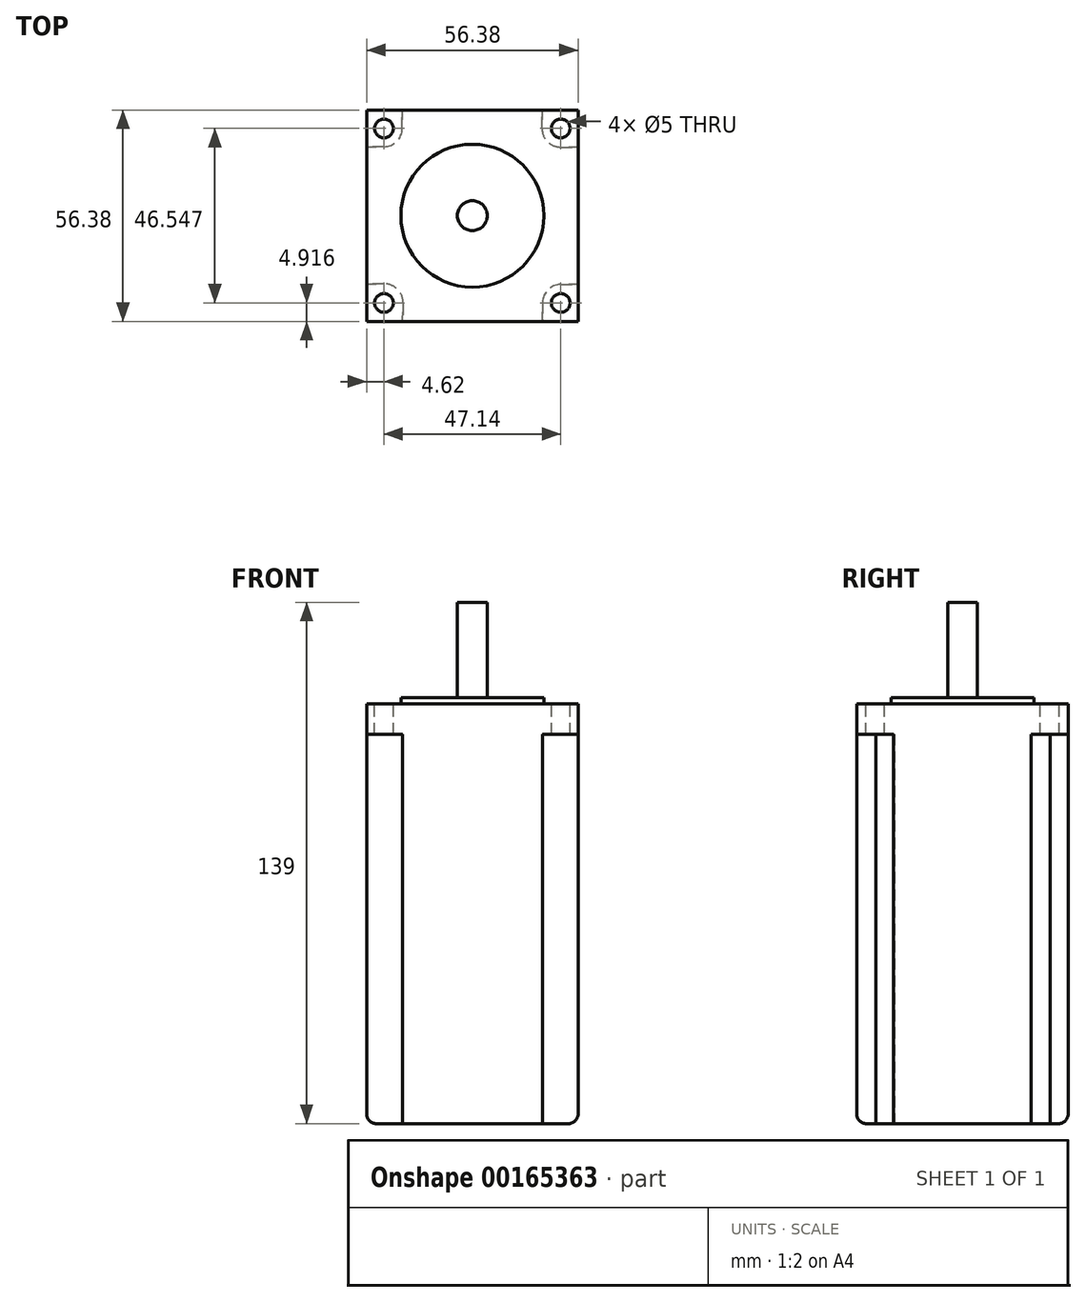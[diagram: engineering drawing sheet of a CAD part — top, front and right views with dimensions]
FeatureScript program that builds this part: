
annotation { "Feature Type Name" : "Feature", "Feature Type Description" : "" }
export const myFeature = defineFeature(function(context is Context, id is Id, definition is map)
    precondition{}
    {
        {
            var Q0;
            Q0=qCreatedBy(makeId("Top.planeOp"),FACE);
            var sketch = newSketch(context, id + "F0", { "sketchPlane" : qUnion([Q0])});
            skLineSegment(sketch, "E0.rect.bottom", {"start": v(28.2, -28.2) * mm, "end": v(-28.2, -28.2) * mm});
            skLineSegment(sketch, "E0.rect.top", {"start": v(28.2, 28.2) * mm, "end": v(-28.2, 28.2) * mm});
            skLineSegment(sketch, "E0.rect.left", {"start": v(28.2, -28.2) * mm, "end": v(28.2, 28.2) * mm});
            skLineSegment(sketch, "E0.rect.right", {"start": v(-28.2, -28.2) * mm, "end": v(-28.2, 28.2) * mm});
            skPoint(sketch, "E0.rect.middle", {"position": v(0, 0) * mm});
            skSolve(sketch);
        }
        {
            var Q0;
            Q0=qSketchRegion(id+"F0",true);
            extrude(context, id + "F1", {"entities" : qUnion([Q0]), "depth" : 112 * mm});
        }
        {
            var Q0;
            Q0=makeQuery(id+"F1.opExtrude","CAP_FACE",FACE,{"disambiguationData":[OSD([sQuery(id+"F0.wireOp",EDGE,"E0.rect.bottom"),sQuery(id+"F0.wireOp",EDGE,"E0.rect.top"),sQuery(id+"F0.wireOp",EDGE,"E0.rect.left"),sQuery(id+"F0.wireOp",EDGE,"E0.rect.right")])],"isStart":false});
            var sketch = newSketch(context, id + "F2", { "sketchPlane" : qUnion([Q0])});
            skLineSegment(sketch, "E1.rect.bottom", {"start": v(23.57, 23.27) * mm, "end": v(-23.57, 23.27) * mm, "construction": true});
            skLineSegment(sketch, "E1.rect.top", {"start": v(23.57, -23.27) * mm, "end": v(-23.57, -23.27) * mm, "construction": true});
            skLineSegment(sketch, "E1.rect.left", {"start": v(23.57, 23.27) * mm, "end": v(23.57, -23.27) * mm, "construction": true});
            skLineSegment(sketch, "E1.rect.right", {"start": v(-23.57, 23.27) * mm, "end": v(-23.57, -23.27) * mm, "construction": true});
            skPoint(sketch, "E1.rect.middle", {"position": v(0, 0) * mm});
            skCircle(sketch, "E2", {"center": v(-23.57, 23.27) * mm, "radius": 2.5 * mm});
            skCircle(sketch, "E3", {"center": v(23.57, 23.27) * mm, "radius": 2.5 * mm});
            skCircle(sketch, "E4", {"center": v(23.57, -23.27) * mm, "radius": 2.5 * mm});
            skCircle(sketch, "E5", {"center": v(-23.57, -23.27) * mm, "radius": 2.5 * mm});
            skSolve(sketch);
        }
        {
            var Q0;
            Q0=qSketchRegion(id+"F2",true);
            extrude(context, id + "F3", {"entities" : qUnion([Q0]), "operationType" : NewBodyOperationType.REMOVE, "endBound" : BoundingType.THROUGH_ALL, "oppositeDirection" : true, "depth" : 25.4 * mm});
        }
        {
            var Q0;
            Q0=makeQuery(id+"F1.opExtrude","CAP_FACE",FACE,{"disambiguationData":[OSD([sQuery(id+"F0.wireOp",EDGE,"E0.rect.bottom"),sQuery(id+"F0.wireOp",EDGE,"E0.rect.top"),sQuery(id+"F0.wireOp",EDGE,"E0.rect.left"),sQuery(id+"F0.wireOp",EDGE,"E0.rect.right")])],"isStart":false});
            var sketch = newSketch(context, id + "F4", { "sketchPlane" : qUnion([Q0])});
            skCircle(sketch, "E6", {"center": v(0, 0) * mm, "radius": 19.05 * mm});
            skSolve(sketch);
        }
        {
            var Q0;
            Q0=qSketchRegion(id+"F4",true);
            extrude(context, id + "F5", {"entities" : qUnion([Q0]), "operationType" : NewBodyOperationType.ADD, "depth" : 1.6 * mm});
        }
        {
            var Q0;
            Q0=makeQuery(id+"F5.opExtrude","CAP_FACE",FACE,{"disambiguationData":[OSD([sQuery(id+"F4.wireOp",EDGE,"E6")])],"isStart":false});
            var sketch = newSketch(context, id + "F6", { "sketchPlane" : qUnion([Q0])});
            skCircle(sketch, "E7", {"center": v(0, 0) * mm, "radius": 3.97 * mm});
            skSolve(sketch);
        }
        {
            var Q0;
            Q0=qSketchRegion(id+"F6",true);
            extrude(context, id + "F7", {"entities" : qUnion([Q0]), "operationType" : NewBodyOperationType.ADD, "depth" : 25.4 * mm});
        }
        {
            var Q0;
            Q0=makeQuery(id+"F1.opExtrude","CAP_FACE",FACE,{"disambiguationData":[OSD([sQuery(id+"F0.wireOp",EDGE,"E0.rect.bottom"),sQuery(id+"F0.wireOp",EDGE,"E0.rect.top"),sQuery(id+"F0.wireOp",EDGE,"E0.rect.left"),sQuery(id+"F0.wireOp",EDGE,"E0.rect.right")])],"isStart":true});
            var sketch = newSketch(context, id + "F8", { "sketchPlane" : qUnion([Q0])});
            skCircle(sketch, "E8", {"center": v(-23.57, 23.27) * mm, "radius": 5.12 * mm, "construction": true});
            skCircle(sketch, "E9", {"center": v(23.57, 23.27) * mm, "radius": 4.9 * mm, "construction": true});
            skCircle(sketch, "E10", {"center": v(23.57, -23.27) * mm, "radius": 5 * mm, "construction": true});
            skCircle(sketch, "E11", {"center": v(-23.57, -23.27) * mm, "radius": 4.87 * mm, "construction": true});
            skLineSegment(sketch, "E12", {"start": v(-18.46, 23.44) * mm, "end": v(-18.61, 28.2) * mm});
            skLineSegment(sketch, "E13", {"start": v(-23.6, 18.16) * mm, "end": v(-28.2, 18.16) * mm});
            skArc(sketch, "E14", {"start": v(-23.6, 18.16) * mm, "mid": v(-19.91, 19.71) * mm, "end": v(-18.46, 23.44) * mm});
            skLineSegment(sketch, "E15", {"start": v(-28.2, 18.16) * mm, "end": v(-28.2, 28.2) * mm});
            skLineSegment(sketch, "E16", {"start": v(-28.2, 28.2) * mm, "end": v(-18.61, 28.2) * mm});
            skLineSegment(sketch, "E17", {"start": v(-18.7, -23.27) * mm, "end": v(-18.7, -28.2) * mm});
            skLineSegment(sketch, "E18", {"start": v(-18.7, -28.2) * mm, "end": v(-19.13, -28.28) * mm});
            skLineSegment(sketch, "E19", {"start": v(-23.57, -18.4) * mm, "end": v(-28.2, -18.4) * mm});
            skLineSegment(sketch, "E20", {"start": v(18.58, -23.35) * mm, "end": v(18.58, -28.2) * mm});
            skLineSegment(sketch, "E21", {"start": v(23.57, -18.28) * mm, "end": v(28.2, -18.28) * mm});
            skLineSegment(sketch, "E22", {"start": v(18.66, 23.15) * mm, "end": v(18.66, 28.2) * mm});
            skLineSegment(sketch, "E23", {"start": v(23.57, 18.37) * mm, "end": v(28.2, 18.37) * mm});
            skLineSegment(sketch, "E24", {"start": v(18.66, 28.2) * mm, "end": v(28.2, 28.2) * mm});
            skLineSegment(sketch, "E25", {"start": v(28.2, 18.37) * mm, "end": v(28.2, 28.2) * mm});
            skLineSegment(sketch, "E26", {"start": v(-28.2, -18.4) * mm, "end": v(-28.2, -28.2) * mm});
            skLineSegment(sketch, "E27", {"start": v(-28.2, -28.2) * mm, "end": v(-18.7, -28.2) * mm});
            skLineSegment(sketch, "E28", {"start": v(18.58, -28.2) * mm, "end": v(28.2, -28.2) * mm});
            skLineSegment(sketch, "E29", {"start": v(28.2, -28.2) * mm, "end": v(28.2, -18.28) * mm});
            skArc(sketch, "E30", {"start": v(-18.7, -23.27) * mm, "mid": v(-20.13, -19.83) * mm, "end": v(-23.57, -18.4) * mm});
            skArc(sketch, "E31", {"start": v(23.57, -18.28) * mm, "mid": v(20, -19.77) * mm, "end": v(18.58, -23.35) * mm});
            skArc(sketch, "E32", {"start": v(18.66, 23.15) * mm, "mid": v(20.14, 19.76) * mm, "end": v(23.57, 18.37) * mm});
            skSolve(sketch);
        }
        {
            var Q0;
            Q0=qSketchRegion(id+"F8",true);
            extrude(context, id + "F9", {"entities" : qUnion([Q0]), "operationType" : NewBodyOperationType.REMOVE, "oppositeDirection" : true, "depth" : 103.89 * mm});
        }
        {
            var Q0;
            Q0=makeQuery(id+"F1.opExtrude","CAP_EDGE",EDGE,{"disambiguationData":[OSD([sQuery(id+"F0.wireOp",EDGE,"E0.rect.right")])],"isStart":true});
            var Q1;
            Q1=makeQuery(id+"F1.opExtrude","CAP_EDGE",EDGE,{"disambiguationData":[OSD([sQuery(id+"F0.wireOp",EDGE,"E0.rect.bottom")])],"isStart":true});
            var Q2;
            Q2=makeQuery(id+"F1.opExtrude","CAP_EDGE",EDGE,{"disambiguationData":[OSD([sQuery(id+"F0.wireOp",EDGE,"E0.rect.left")])],"isStart":true});
            var Q3;
            Q3=makeQuery(id+"F1.opExtrude","CAP_EDGE",EDGE,{"disambiguationData":[OSD([sQuery(id+"F0.wireOp",EDGE,"E0.rect.top")])],"isStart":true});
            fillet(context, id + "F10", {"entities" : qUnion([Q0, Q1, Q2, Q3]), "radius" : 2.54 * mm, "tangentPropagation" : true, "allowEdgeOverflow" : false});
        }
    });
